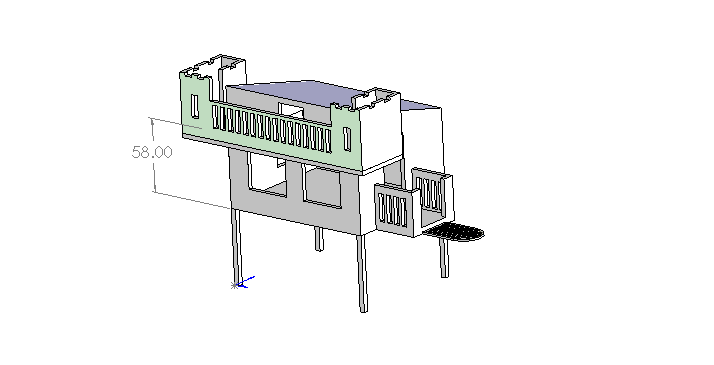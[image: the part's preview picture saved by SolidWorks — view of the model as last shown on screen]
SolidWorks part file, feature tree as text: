
SOLIDWORKS PART (.sldprt)
format: sldprt  version: not decoded by parser v0  size: 946,688 bytes
history: native  units: mm
features: sketch x21, cut_extrude x13, extrude x8, plane x3, shell x1 + 1 further entry (+10 scaffold rows collapsed)
feature tree (57):
  "Annotations"  RD1=1473.2mm
  scaffold x10  (default folders/planes/origin — collapsed)
  sketch  "Sketch1"  dims[c1.D1=101.6mm c1.D2=101.6mm c2.D1=101.6mm c2.D2=101.6mm c2.D3=90.0deg c2.D4=2438.4mm]
  extrude  "Extrude1"  Depth=1524mm
  sketch  "Sketch4"  dims[D1=2438.4mm D2=1828.8mm]
  extrude  "Extrude5"  [1 undecoded]
  shell  "Shell4"  Thickness=88.9mm
  sketch  "Sketch5"  dims[D1=914.4mm D2=914.4mm D3=457.2mm D4=914.4mm D5=914.4mm D6=457.2mm D7=457.2mm D8=914.4mm]
  cut_extrude  "Cut-Extrude1"  Depth=127mm
  plane  "Plane1"
  sketch  "Sketch6"  dims[c1.D1=914.4mm c1.D2=914.4mm c1.D3=762.0mm c1.D4=457.2mm c2.D3=304.8mm]
  cut_extrude  "Cut-Extrude2"  Depth=127mm
  sketch  "Sketch7"  dims[D1=457.2mm D2=914.4mm D3=914.4mm D4=304.8mm]
  cut_extrude  "Cut-Extrude3"  Depth=127mm
  plane  "Plane2"  Offset=2997.2mm
  plane  "Plane3"
  sketch  "Sketch8"  dims[D1=609.6mm D2=609.6mm D3=609.6mm D4=1219.2mm]
  extrude  "Extrude6"  Depth=88.9mm
  sketch  "Sketch9"  dims[D1=88.9mm]
  extrude  "Extrude7"  Depth=1219.2mm
  sketch  "Sketch10"  dims[c1.D1=3048.0mm c1.D2=711.2mm c1.D3=457.2mm c2.D1=711.2mm]
  cut_extrude  "Cut-Extrude4"  Depth=1016mm
  sketch  "Sketch11"  dims[D1=1524.0mm D2=609.6mm D3=152.4mm D4=762.0mm]
  cut_extrude  "Cut-Extrude5"  Depth=127mm
  sketch  "Sketch12"  dims[D1=3149.6mm]
  extrude  "Extrude8"  Depth=127mm
  sketch  "Sketch13"  dims[D1=914.4mm D2=1219.2mm D3=457.2mm]
  extrude  "Extrude9"  Depth=127mm
  sketch  "Sketch14"  dims[D1=88.9mm D2=88.9mm D3=88.9mm D4=711.2mm D5=254.0mm]
  extrude  "Extrude10"  Depth=762mm
  sketch  "Sketch15"  dims[D1=762.0mm]
  extrude  "Extrude11"  Depth=38.1mm
  sketch  "Sketch16"  dims[D1=609.6mm D2=762.0mm]
  cut_extrude  "Cut-Extrude6"  Depth=205.74mm
  sketch  "Sketch17"  dims[D1=152.4mm D2=152.4mm D3=152.4mm D4=152.4mm D5=152.4mm D6=152.4mm D7=127.0mm D8=127.0mm D9=152.4mm]
  cut_extrude  "Cut-Extrude8"  Depth=127mm
  sketch  "Sketch18"  dims[D1=152.4mm D2=152.4mm D3=304.8mm D4=304.8mm]
  cut_extrude  "Cut-Extrude9"  [1 undecoded]
  sketch  "Sketch19"  dims[c1.D1=152.4mm c1.D2=152.4mm c2.D1=114.3mm c2.D2=457.2mm c2.D3=558.8mm]
  cut_extrude  "Cut-Extrude10"  Depth=127mm
  sketch  "Sketch20"  dims[D1=152.4mm D2=152.4mm D3=254.0mm D4=254.0mm D5=355.6mm D6=457.2mm]
  cut_extrude  "Cut-Extrude11"  Depth=127mm
  sketch  "Sketch21"
  cut_extrude  "Cut-Extrude12"  [1 undecoded]
  sketch  "Sketch22"
  cut_extrude  "Cut-Extrude14"  Depth=127mm
  sketch  "Sketch23"
  cut_extrude  "Cut-Extrude15"  Depth=127mm
decode coverage: 37 of 43 modeling features carry decoded parameters; 1 rows unclassified (native names shown)
note: 3 parameter values undecoded
summary: no parameter record found for 3 features
note: suppression state not decoded; provenance and decode notes live in map.json
